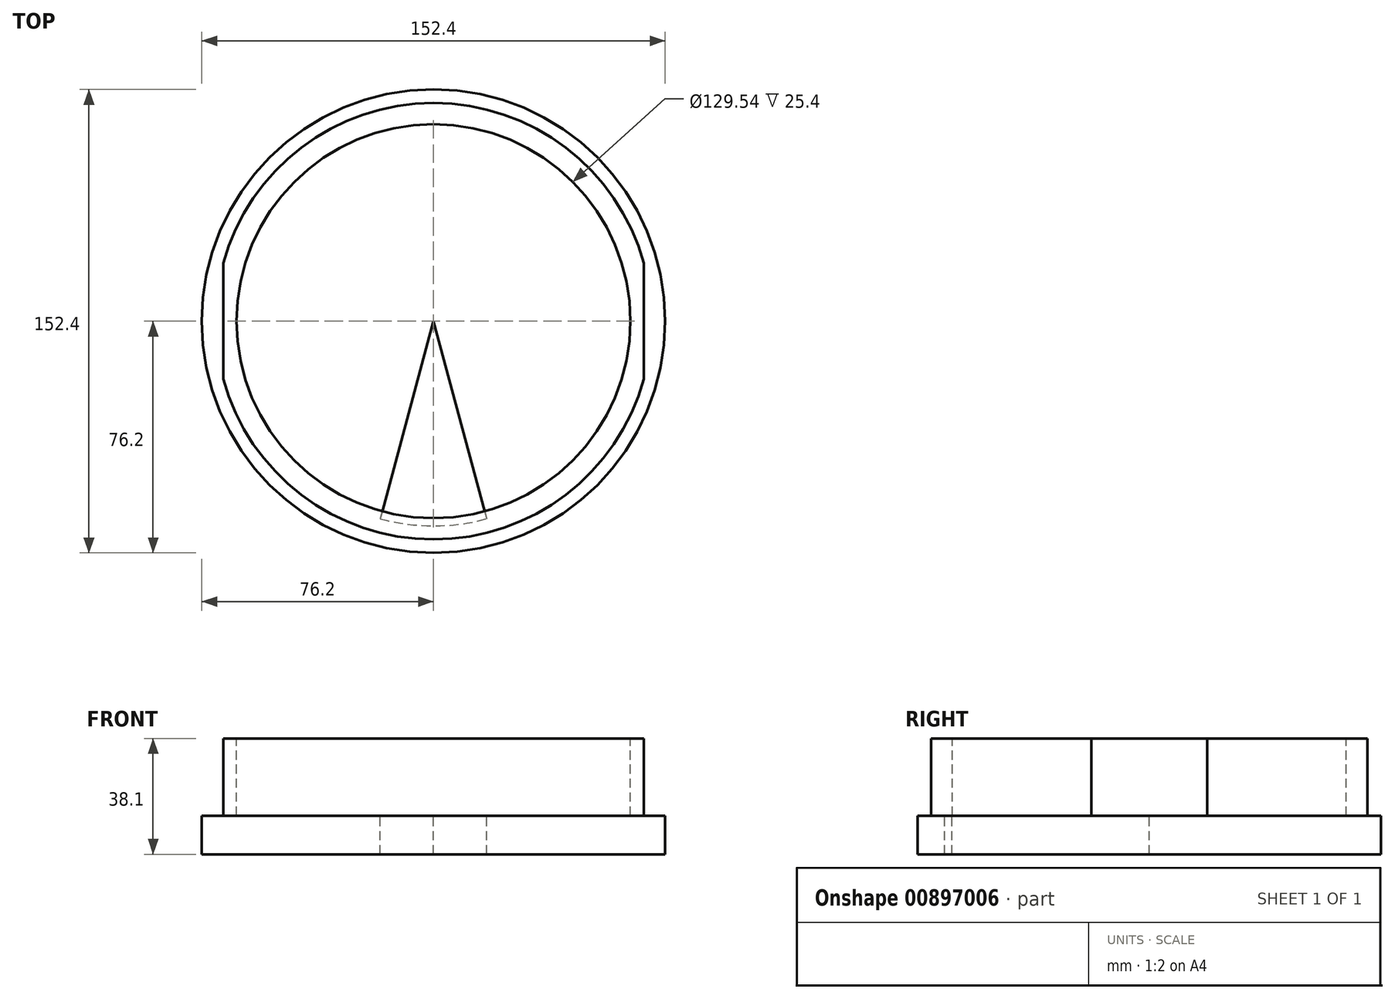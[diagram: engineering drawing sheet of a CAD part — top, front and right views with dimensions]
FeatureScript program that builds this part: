
annotation { "Feature Type Name" : "Feature", "Feature Type Description" : "" }
export const myFeature = defineFeature(function(context is Context, id is Id, definition is map)
    precondition{}
    {
        {
            var Q0;
            Q0=qCreatedBy(makeId("Top.planeOp"),FACE);
            var sketch = newSketch(context, id + "F0", { "sketchPlane" : qUnion([Q0])});
            skCircle(sketch, "E0", {"center": v(0, 0) * mm, "radius": 76.2 * mm});
            skSolve(sketch);
        }
        {
            var Q0;
            Q0=qSketchRegion(id+"F0",true);
            extrude(context, id + "F1", {"entities" : qUnion([Q0]), "oppositeDirection" : true, "depth" : 88.9 * mm, "offsetDistance" : 25.4 * mm});
        }
        {
            var Q0;
            Q0=makeQuery(id+"F0.imprint","IMPRINT",FACE,{"disambiguationData":[TD([[makeQuery(id+"F0.imprint","IMPRINT",EDGE,{"derivedFrom":sQuery(id+"F0.wireOp",EDGE,"E0")}),1.0]])]});
            var sketch = newSketch(context, id + "F2", { "sketchPlane" : qUnion([Q0])});
            skCircle(sketch, "E1", {"center": v(0, 0) * mm, "radius": 71.76 * mm});
            skSolve(sketch);
        }
        {
            var Q0;
            Q0=makeQuery(id+"F2.imprint","IMPRINT",FACE,{"disambiguationData":[TD([[makeQuery(id+"F2.imprint","IMPRINT",EDGE,{"derivedFrom":sQuery(id+"F2.wireOp",EDGE,"E1")}),-1.0]])]});
            extrude(context, id + "F3", {"entities" : qUnion([Q0]), "operationType" : NewBodyOperationType.REMOVE, "oppositeDirection" : true, "depth" : 25.4 * mm, "offsetDistance" : 25.4 * mm});
        }
        {
            var Q0;
            Q0=makeQuery(id+"F0.imprint","IMPRINT",FACE,{"disambiguationData":[TD([[makeQuery(id+"F0.imprint","IMPRINT",EDGE,{"derivedFrom":sQuery(id+"F0.wireOp",EDGE,"E0")}),1.0]])]});
            var sketch = newSketch(context, id + "F4", { "sketchPlane" : qUnion([Q0])});
            skCircle(sketch, "E2", {"center": v(0, 0) * mm, "radius": 64.77 * mm});
            skSolve(sketch);
        }
        {
            var Q0;
            Q0=qSketchRegion(id+"F4",true);
            extrude(context, id + "F5", {"entities" : qUnion([Q0]), "operationType" : NewBodyOperationType.REMOVE, "oppositeDirection" : true, "depth" : 25.4 * mm, "offsetDistance" : 25.4 * mm});
        }
        {
            var Q0;
            Q0=qCreatedBy(makeId("Top.planeOp"),FACE);
            cPlane(context, id + "F6", {"entities" : qUnion([Q0]), "cplaneType" : CPlaneType.OFFSET, "offset" : 25.4 * mm, "oppositeDirection" : true, "width" : 152.4 * mm, "height" : 152.4 * mm});
        }
        {
            var Q0;
            Q0=qCreatedBy(id+"F6.planeOp",FACE);
            var sketch = newSketch(context, id + "F7", { "sketchPlane" : qUnion([Q0])});
            skLineSegment(sketch, "E3", {"start": v(0, 0) * mm, "end": v(-17.53, -64.99) * mm});
            skLineSegment(sketch, "E4", {"start": v(0, 0) * mm, "end": v(17.53, -64.99) * mm});
            skArc(sketch, "E5", {"start": v(17.53, -64.99) * mm, "mid": v(0, -67.31) * mm, "end": v(-17.53, -64.99) * mm});
            skLineSegment(sketch, "E6", {"start": v(0, -67.31) * mm, "end": v(-17.53, -64.99) * mm, "construction": true});
            skLineSegment(sketch, "E7", {"start": v(0, -67.3) * mm, "end": v(17.53, -64.99) * mm, "construction": true});
            skSolve(sketch);
        }
        {
            var Q0;
            Q0=qCreatedBy(makeId("Front.planeOp"),FACE);
            cPlane(context, id + "F8", {"entities" : qUnion([Q0]), "cplaneType" : CPlaneType.OFFSET, "offset" : 78.74 * mm, "width" : 152.4 * mm, "height" : 152.4 * mm});
        }
        {
            var Q0;
            Q0=qCreatedBy(makeId("Front.planeOp"),FACE);
            cPlane(context, id + "F9", {"entities" : qUnion([Q0]), "cplaneType" : CPlaneType.OFFSET, "offset" : 76.2 * mm, "width" : 152.4 * mm, "height" : 152.4 * mm});
        }
        {
            var Q0;
            Q0=qCreatedBy(id+"F9.planeOp",FACE);
            var sketch = newSketch(context, id + "F10", { "sketchPlane" : qUnion([Q0])});
            skLineSegment(sketch, "E8", {"start": v(0, -69.85) * mm, "end": v(0, 0) * mm, "construction": true});
            skArc(sketch, "E9", {"start": v(8.9, -69.85) * mm, "mid": v(6.29, -76.14) * mm, "end": v(0, -78.74) * mm});
            skArc(sketch, "E10.MirrorCS", {"start": v(-8.9, -69.85) * mm, "mid": v(-6.29, -76.14) * mm, "end": v(0, -78.74) * mm});
            skLineSegment(sketch, "E11", {"start": v(-8.9, -69.85) * mm, "end": v(8.9, -69.85) * mm});
            skSolve(sketch);
        }
        {
            var Q0;
            Q0=qSketchRegion(id+"F7",true);
            extrude(context, id + "F11", {"entities" : qUnion([Q0]), "operationType" : NewBodyOperationType.REMOVE, "endBound" : BoundingType.THROUGH_ALL, "oppositeDirection" : true, "depth" : 25.4 * mm, "offsetDistance" : 25.4 * mm});
        }
        {
            var Q0;
            Q0=makeQuery(id+"F1.opExtrude","CAP_FACE",FACE,{"disambiguationData":[OSD([sQuery(id+"F0.wireOp",EDGE,"E0")])],"isStart":true});
            var sketch = newSketch(context, id + "F12", { "sketchPlane" : qUnion([Q0])});
            skLineSegment(sketch, "E12", {"start": v(71.76, 0) * mm, "end": v(-71.76, 0) * mm, "construction": true});
            skLineSegment(sketch, "E13", {"start": v(69.18, 19.05) * mm, "end": v(69.18, 0) * mm});
            skLineSegment(sketch, "E14", {"start": v(69.18, 0) * mm, "end": v(69.18, -19.05) * mm});
            skLineSegment(sketch, "E15", {"start": v(0, 19.89) * mm, "end": v(0, -23.04) * mm, "construction": true});
            skLineSegment(sketch, "E16.MirrorCS", {"start": v(-69.18, 19.05) * mm, "end": v(-69.18, 0) * mm});
            skLineSegment(sketch, "E17.MirrorCS", {"start": v(-69.18, 0) * mm, "end": v(-69.18, -19.05) * mm});
            skSolve(sketch);
        }
        {
            var Q0;
            {var subQ0=sQuery(id+"F12.wireOp",EDGE,"E16.MirrorCS");Q0=makeQuery(id+"F12.imprint","IMPRINT",FACE,{"disambiguationData":[TD([[makeQuery(id+"F12.imprint","IMPRINT",EDGE,{"derivedFrom":subQ0}),-1.0]])]});}
            var Q1;
            {var subQ0=sQuery(id+"F12.wireOp",EDGE,"E13");Q1=makeQuery(id+"F12.imprint","IMPRINT",FACE,{"disambiguationData":[TD([[makeQuery(id+"F12.imprint","IMPRINT",EDGE,{"derivedFrom":subQ0}),1.0]])]});}
            extrude(context, id + "F13", {"entities" : qUnion([Q0, Q1]), "operationType" : NewBodyOperationType.REMOVE, "oppositeDirection" : true, "depth" : 25.4 * mm, "offsetDistance" : 25.4 * mm});
        }
        {
            var Q0;
            Q0=makeQuery(id+"F1.opExtrude","CAP_FACE",FACE,{"disambiguationData":[OSD([sQuery(id+"F0.wireOp",EDGE,"E0")])],"isStart":false});
            var sketch = newSketch(context, id + "F14", { "sketchPlane" : qUnion([Q0])});
            skCircle(sketch, "E18", {"center": v(0, 0) * mm, "radius": 106.31 * mm});
            skSolve(sketch);
        }
        {
            var Q0;
            Q0 = qSketchRegion(id + "F14", true);
            extrude(context, id + "F15", {"entities" : qUnion([Q0]), "operationType" : NewBodyOperationType.REMOVE, "oppositeDirection" : true, "depth" : 50.8 * mm, "offsetDistance" : 25.4 * mm});
        }
    });
